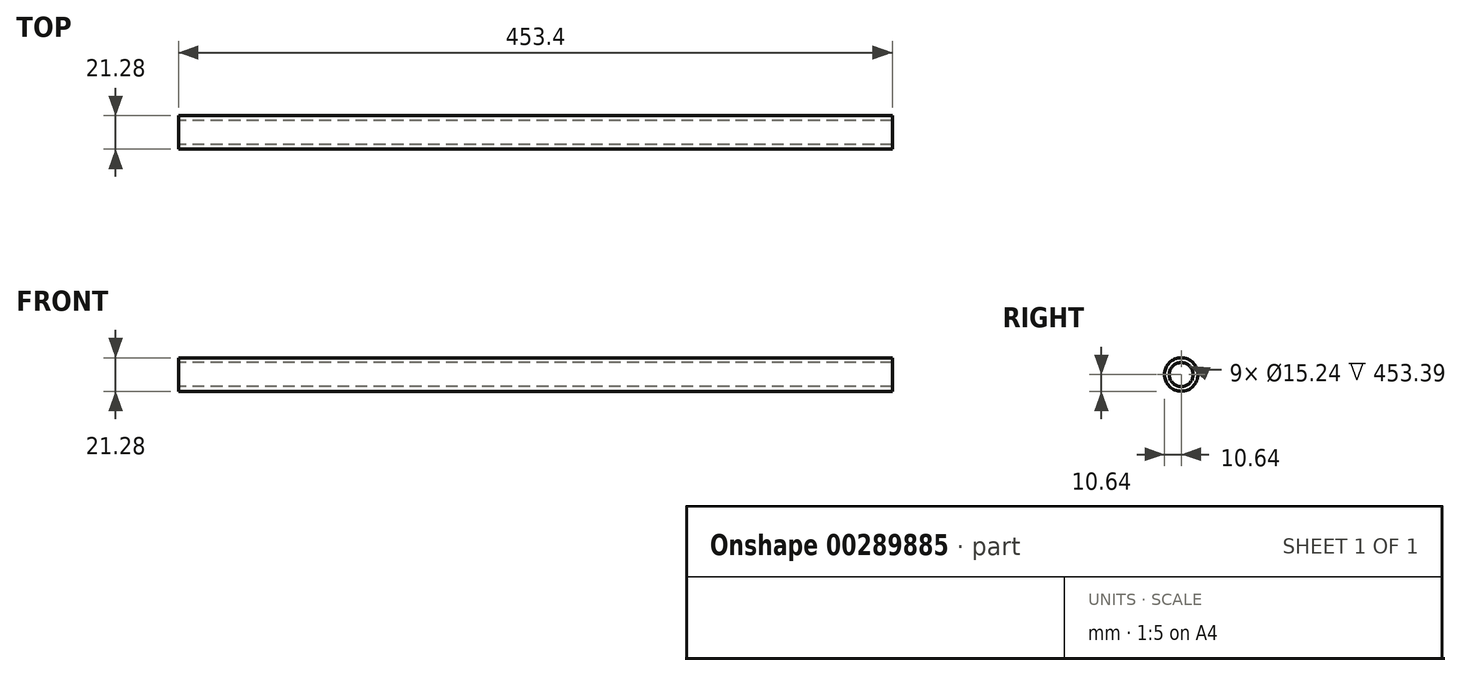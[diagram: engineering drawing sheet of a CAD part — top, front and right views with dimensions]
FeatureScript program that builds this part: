
annotation { "Feature Type Name" : "Feature", "Feature Type Description" : "" }
export const myFeature = defineFeature(function(context is Context, id is Id, definition is map)
    precondition{}
    {
        {
            var Q0;
            Q0=qCreatedBy(makeId("Right.planeOp"),FACE);
            var sketch = newSketch(context, id + "F0", { "sketchPlane" : qUnion([Q0])});
            skCircle(sketch, "E0", {"center": v(0, 0) * mm, "radius": 7.62 * mm});
            skCircle(sketch, "E1", {"center": v(0, 0) * mm, "radius": 10.64 * mm});
            skSolve(sketch);
        }
        {
            var Q0;
            Q0=makeQuery(id+"F0.imprint","IMPRINT",FACE,{"disambiguationData":[TD([[makeQuery(id+"F0.imprint","IMPRINT",EDGE,{"derivedFrom":sQuery(id+"F0.wireOp",EDGE,"E0")}),-1.0]])]});
            extrude(context, id + "F1", {"entities" : qUnion([Q0]), "endBound" : BoundingType.SYMMETRIC, "depth" : 393.7 * mm + 59.69 * mm});
        }
    });
